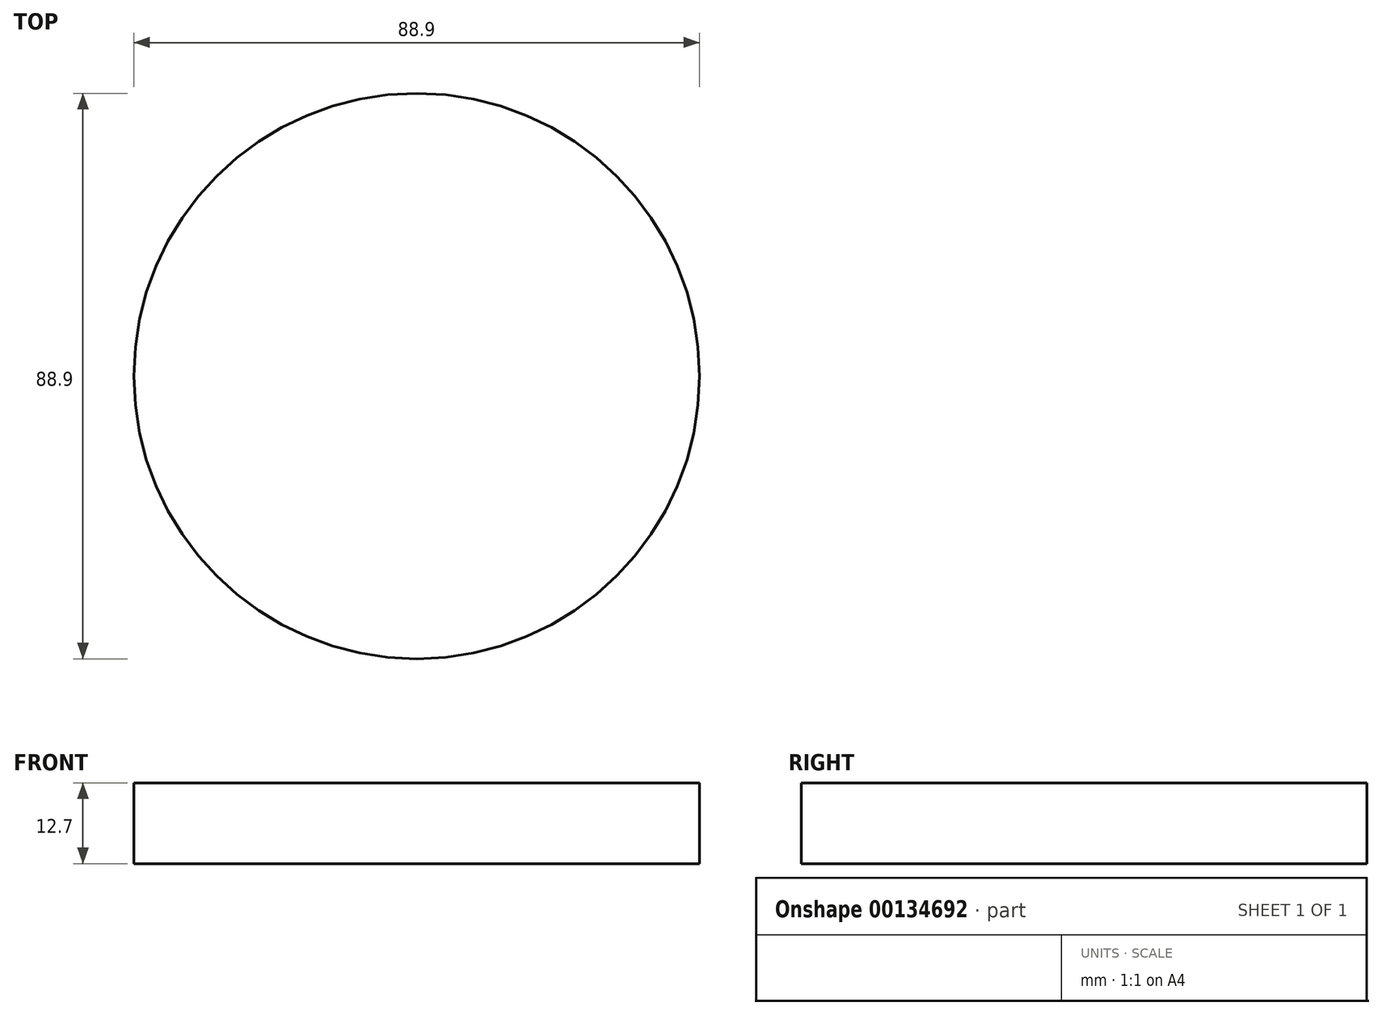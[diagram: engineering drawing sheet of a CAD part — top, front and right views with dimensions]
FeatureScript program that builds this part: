
annotation { "Feature Type Name" : "Feature", "Feature Type Description" : "" }
export const myFeature = defineFeature(function(context is Context, id is Id, definition is map)
    precondition{}
    {
        {
            var Q0;
            Q0=qCreatedBy(makeId("Top.planeOp"),FACE);
            var sketch = newSketch(context, id + "F0", { "sketchPlane" : qUnion([Q0])});
            skCircle(sketch, "E0", {"center": v(0, 0) * mm, "radius": 44.45 * mm});
            skSolve(sketch);
        }
        {
            var Q0;
            Q0 = qSketchRegion(id + "F0", true);
            var Q1;
            Q1=makeQuery(id+"F0.imprint","IMPRINT",FACE,{"disambiguationData":[TD([[makeQuery(id+"F0.imprint","IMPRINT",EDGE,{"derivedFrom":sQuery(id+"F0.wireOp",EDGE,"E0")}),1.0]])]});
            extrude(context, id + "F1", {"entities" : qUnion([Q0, Q1]), "depth" : 12.7 * mm});
        }
    });
